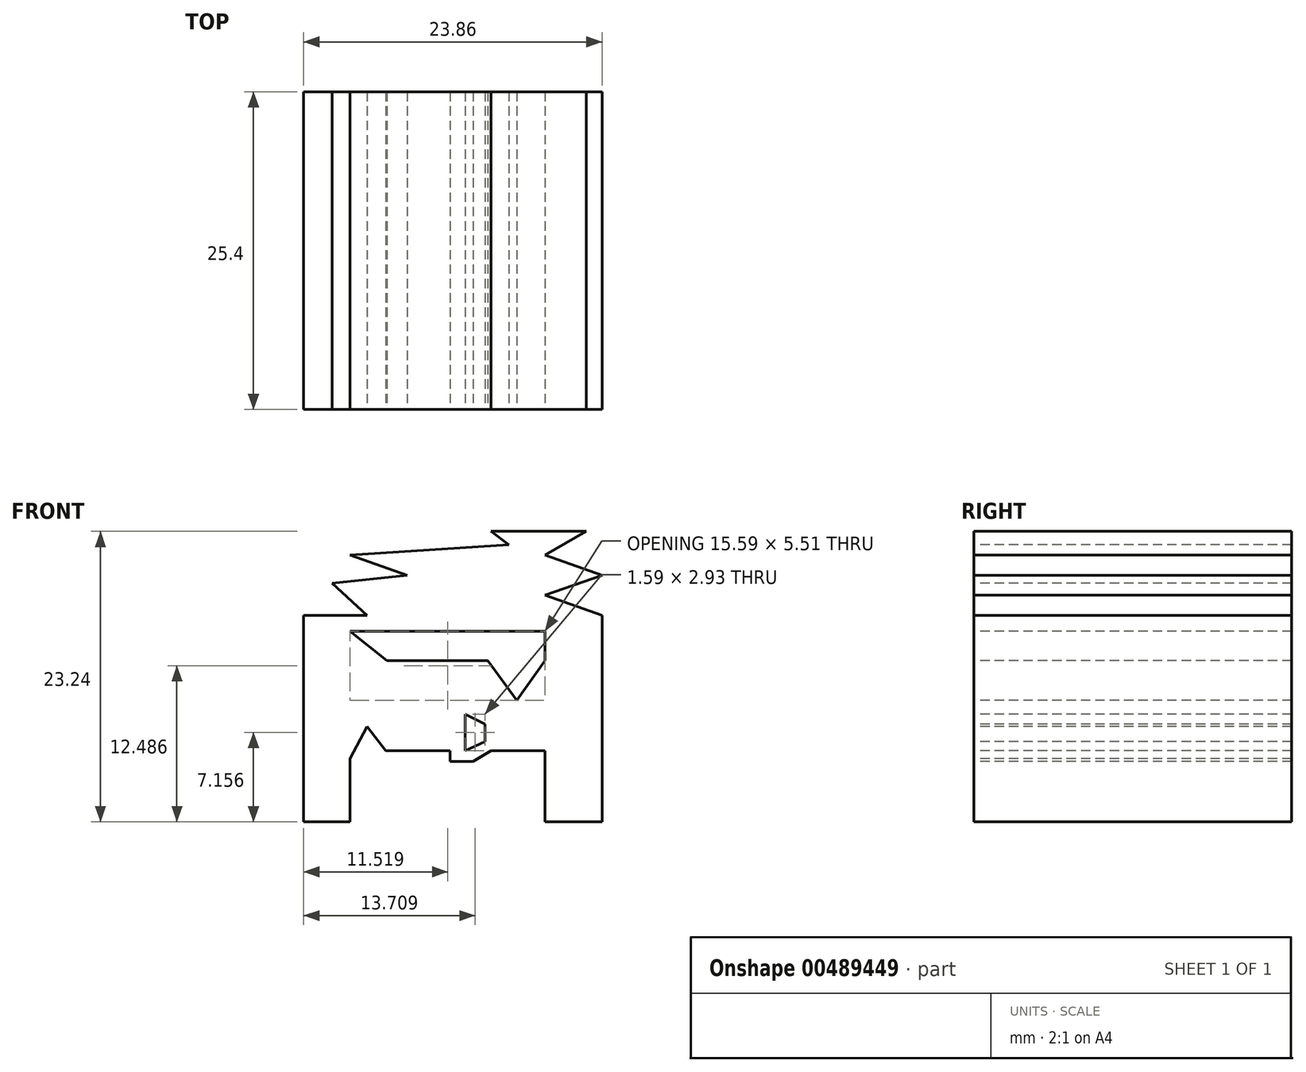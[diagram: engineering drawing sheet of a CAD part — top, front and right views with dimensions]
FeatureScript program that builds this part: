
annotation { "Feature Type Name" : "Feature", "Feature Type Description" : "" }
export const myFeature = defineFeature(function(context is Context, id is Id, definition is map)
    precondition{}
    {
        {
            var Q0;
            Q0=qCreatedBy(makeId("Front.planeOp"),FACE);
            var sketch = newSketch(context, id + "F0", { "sketchPlane" : qUnion([Q0])});
            skLineSegment(sketch, "E0", {"start": v(0, 0) * mm, "end": v(0, 25.4) * mm});
            skLineSegment(sketch, "E1", {"start": v(0, 25.4) * mm, "end": v(25.4, 25.4) * mm});
            skLineSegment(sketch, "E2", {"start": v(25.4, 25.4) * mm, "end": v(25.4, 0) * mm});
            skLineSegment(sketch, "E3", {"start": v(25.4, 0) * mm, "end": v(0, 0) * mm});
            skSolve(sketch);
        }
        {
            var Q0;
            Q0=makeQuery(id+"F0.imprint","IMPRINT",FACE,{"disambiguationData":[TD([[makeQuery(id+"F0.imprint","IMPRINT",EDGE,{"derivedFrom":sQuery(id+"F0.wireOp",EDGE,"E0")}),-1.0]])]});
            var sketch = newSketch(context, id + "F1", { "sketchPlane" : qUnion([Q0])});
            skPoint(sketch, "E4.start.orphan", {"position": v(21.67, 15.08) * mm});
            skPoint(sketch, "E5.end.orphan", {"position": v(25.16, 15.08) * mm});
            skLineSegment(sketch, "E6", {"start": v(0, 0) * mm, "end": v(0, 16.51) * mm});
            skLineSegment(sketch, "E7", {"start": v(0, 16.51) * mm, "end": v(5.08, 16.51) * mm});
            skLineSegment(sketch, "E8", {"start": v(5.08, 16.51) * mm, "end": v(2.27, 19.09) * mm});
            skLineSegment(sketch, "E9", {"start": v(2.27, 19.09) * mm, "end": v(8.28, 19.73) * mm});
            skLineSegment(sketch, "E10", {"start": v(8.28, 19.73) * mm, "end": v(3.73, 21.34) * mm});
            skLineSegment(sketch, "E11", {"start": v(3.73, 21.34) * mm, "end": v(16.4, 22.18) * mm});
            skLineSegment(sketch, "E12", {"start": v(16.4, 22.18) * mm, "end": v(15, 23.24) * mm});
            skLineSegment(sketch, "E13", {"start": v(15, 23.24) * mm, "end": v(22.61, 23.24) * mm});
            skLineSegment(sketch, "E14", {"start": v(22.61, 23.24) * mm, "end": v(19.31, 21.34) * mm});
            skLineSegment(sketch, "E15", {"start": v(19.31, 21.34) * mm, "end": v(23.86, 19.73) * mm});
            skLineSegment(sketch, "E16", {"start": v(23.86, 19.73) * mm, "end": v(19.31, 18.12) * mm});
            skLineSegment(sketch, "E17", {"start": v(19.31, 18.12) * mm, "end": v(23.86, 16.51) * mm});
            skLineSegment(sketch, "E18", {"start": v(23.86, 16.51) * mm, "end": v(23.86, 0) * mm});
            skLineSegment(sketch, "E19", {"start": v(23.86, 0) * mm, "end": v(19.31, 0) * mm});
            skLineSegment(sketch, "E20", {"start": v(19.31, 0) * mm, "end": v(19.31, 15.24) * mm});
            skLineSegment(sketch, "E21", {"start": v(19.31, 15.24) * mm, "end": v(9.08, 15.24) * mm});
            skLineSegment(sketch, "E22", {"start": v(3.73, 0) * mm, "end": v(0, 0) * mm});
            skLineSegment(sketch, "E23", {"start": v(9.08, 15.24) * mm, "end": v(3.73, 15.24) * mm});
            skLineSegment(sketch, "E24", {"start": v(3.73, 15.24) * mm, "end": v(3.73, 0) * mm});
            skPoint(sketch, "E25.orphan", {"position": v(9.08, 0) * mm});
            skLineSegment(sketch, "E26", {"start": v(3.73, 15.24) * mm, "end": v(3.73, 9.57) * mm});
            skLineSegment(sketch, "E27", {"start": v(3.73, 9.57) * mm, "end": v(6.65, 9.57) * mm});
            skLineSegment(sketch, "E28", {"start": v(6.65, 9.57) * mm, "end": v(6.65, 12.9) * mm});
            skLineSegment(sketch, "E29", {"start": v(6.65, 12.9) * mm, "end": v(3.73, 15.24) * mm});
            skLineSegment(sketch, "E30", {"start": v(6.65, 12.9) * mm, "end": v(9.08, 12.9) * mm});
            skLineSegment(sketch, "E31", {"start": v(9.08, 12.9) * mm, "end": v(9.08, 9.57) * mm});
            skLineSegment(sketch, "E32", {"start": v(9.08, 9.57) * mm, "end": v(12.36, 9.57) * mm});
            skLineSegment(sketch, "E33", {"start": v(12.36, 9.57) * mm, "end": v(12.36, 12.9) * mm});
            skLineSegment(sketch, "E34", {"start": v(12.36, 12.9) * mm, "end": v(9.08, 12.9) * mm});
            skLineSegment(sketch, "E35", {"start": v(12.36, 12.9) * mm, "end": v(14.74, 12.9) * mm});
            skLineSegment(sketch, "E36", {"start": v(14.74, 12.9) * mm, "end": v(14.74, 9.57) * mm});
            skLineSegment(sketch, "E37", {"start": v(3.73, 5.05) * mm, "end": v(5.07, 7.62) * mm});
            skPoint(sketch, "E37.endSnap0", {"position": v(3.73, 7.62) * mm});
            skLineSegment(sketch, "E38", {"start": v(5.07, 7.62) * mm, "end": v(6.57, 5.69) * mm});
            skLineSegment(sketch, "E39", {"start": v(4.4, 6.34) * mm, "end": v(6.07, 6.34) * mm});
            skLineSegment(sketch, "E40", {"start": v(6.57, 5.69) * mm, "end": v(9.19, 5.69) * mm});
            skLineSegment(sketch, "E41", {"start": v(9.19, 5.69) * mm, "end": v(9.19, 8.62) * mm});
            skLineSegment(sketch, "E42", {"start": v(9.19, 8.62) * mm, "end": v(9.19, 5.69) * mm});
            skLineSegment(sketch, "E43", {"start": v(9.19, 5.69) * mm, "end": v(11.73, 5.69) * mm});
            skLineSegment(sketch, "E44", {"start": v(11.73, 5.69) * mm, "end": v(12.92, 5.69) * mm});
            skLineSegment(sketch, "E45", {"start": v(12.92, 5.69) * mm, "end": v(12.92, 8.62) * mm});
            skLineSegment(sketch, "E46", {"start": v(12.92, 8.62) * mm, "end": v(14.5, 7.83) * mm});
            skLineSegment(sketch, "E47", {"start": v(14.5, 7.83) * mm, "end": v(14.5, 6.4) * mm});
            skLineSegment(sketch, "E48", {"start": v(14.5, 6.4) * mm, "end": v(12.92, 5.69) * mm});
            skLineSegment(sketch, "E49", {"start": v(9.08, 12.11) * mm, "end": v(9.08, 10.45) * mm});
            skLineSegment(sketch, "E50", {"start": v(9.08, 10.45) * mm, "end": v(12.36, 10.45) * mm});
            skLineSegment(sketch, "E51", {"start": v(12.36, 10.45) * mm, "end": v(12.36, 11.24) * mm});
            skLineSegment(sketch, "E52", {"start": v(12.36, 11.24) * mm, "end": v(9.08, 12.11) * mm});
            skLineSegment(sketch, "E53", {"start": v(11.73, 5.69) * mm, "end": v(11.73, 8.7) * mm});
            skLineSegment(sketch, "E54", {"start": v(11.73, 8.7) * mm, "end": v(13.55, 9.34) * mm});
            skLineSegment(sketch, "E55", {"start": v(13.55, 9.34) * mm, "end": v(14.98, 8.62) * mm});
            skLineSegment(sketch, "E56", {"start": v(14.98, 8.62) * mm, "end": v(14.98, 5.69) * mm});
            skLineSegment(sketch, "E57", {"start": v(14.98, 5.69) * mm, "end": v(13.55, 4.82) * mm});
            skLineSegment(sketch, "E58", {"start": v(13.55, 4.82) * mm, "end": v(11.73, 4.82) * mm});
            skLineSegment(sketch, "E59", {"start": v(11.73, 5.69) * mm, "end": v(11.73, 4.82) * mm});
            skPoint(sketch, "E60.end.orphan", {"position": v(17.36, 12.9) * mm});
            skLineSegment(sketch, "E61", {"start": v(14.74, 12.9) * mm, "end": v(17.04, 9.73) * mm});
            skLineSegment(sketch, "E62", {"start": v(17.04, 9.73) * mm, "end": v(19.31, 12.9) * mm});
            skLineSegment(sketch, "E63", {"start": v(19.31, 12.9) * mm, "end": v(16.96, 11.32) * mm});
            skPoint(sketch, "E63.endSnap0", {"position": v(18.18, 11.32) * mm});
            skLineSegment(sketch, "E64", {"start": v(16.96, 11.32) * mm, "end": v(14.74, 12.9) * mm});
            skLineSegment(sketch, "E65", {"start": v(14.98, 5.69) * mm, "end": v(19.31, 5.69) * mm});
            skSolve(sketch);
        }
        {
            var Q0;
            Q0=makeQuery(id+"F0.imprint","IMPRINT",FACE,{"disambiguationData":[TD([[makeQuery(id+"F0.imprint","IMPRINT",EDGE,{"derivedFrom":sQuery(id+"F0.wireOp",EDGE,"E0")}),-1.0]])]});
            extrude(context, id + "F2", {"entities" : qUnion([Q0]), "oppositeDirection" : true, "depth" : 25.4 * mm, "offsetDistance" : 25.4 * mm});
        }
        {
            var Q0;
            {var subQ0=sQuery(id+"F1.wireOp",EDGE,"E7");Q0=makeQuery(id+"F1.imprint","IMPRINT",FACE,{"disambiguationData":[TD([[makeQuery(id+"F1.imprint","IMPRINT",EDGE,{"derivedFrom":subQ0}),1.0]])]});}
            var Q1;
            {var subQ1=sQuery(id+"F1.wireOp",EDGE,"E21");Q1=makeQuery(id+"F1.imprint","IMPRINT",FACE,{"disambiguationData":[TD([[makeQuery(id+"F1.imprint","IMPRINT",EDGE,{"derivedFrom":subQ1}),1.0]])]});}
            var Q2;
            {var subQ1=sQuery(id+"F1.wireOp",EDGE,"E39");Q2=makeQuery(id+"F1.imprint","IMPRINT",FACE,{"disambiguationData":[TD([[makeQuery(id+"F1.imprint","IMPRINT",EDGE,{"derivedFrom":subQ1}),-1.0]])]});}
            var Q3;
            Q3=makeQuery(id+"F1.imprint","IMPRINT",FACE,{"disambiguationData":[TD([[makeQuery(id+"F1.imprint","IMPRINT",EDGE,{"derivedFrom":sQuery(id+"F1.wireOp",EDGE,"E45")}),-1.0]])]});
            var Q4;
            Q4=makeQuery(id+"F1.imprint","IMPRINT",FACE,{"disambiguationData":[TD([[makeQuery(id+"F1.imprint","IMPRINT",EDGE,{"derivedFrom":sQuery(id+"F1.wireOp",EDGE,"E49")}),1.0]])]});
            var Q5;
            Q5=makeQuery(id+"F1.imprint","IMPRINT",FACE,{"disambiguationData":[TD([[makeQuery(id+"F1.imprint","IMPRINT",EDGE,{"derivedFrom":sQuery(id+"F1.wireOp",EDGE,"E61")}),1.0]])]});
            var Q6;
            {var subQ3=sQuery(id+"F1.wireOp",EDGE,"E39");Q6=makeQuery(id+"F1.imprint","IMPRINT",FACE,{"disambiguationData":[TD([[makeQuery(id+"F1.imprint","IMPRINT",EDGE,{"derivedFrom":subQ3}),1.0]])]});}
            extrude(context, id + "F3", {"entities" : qUnion([Q0, Q1, Q2, Q3, Q4, Q5, Q6]), "operationType" : NewBodyOperationType.REMOVE, "oppositeDirection" : true, "depth" : 25.4 * mm, "offsetDistance" : 25.4 * mm});
        }
    });
